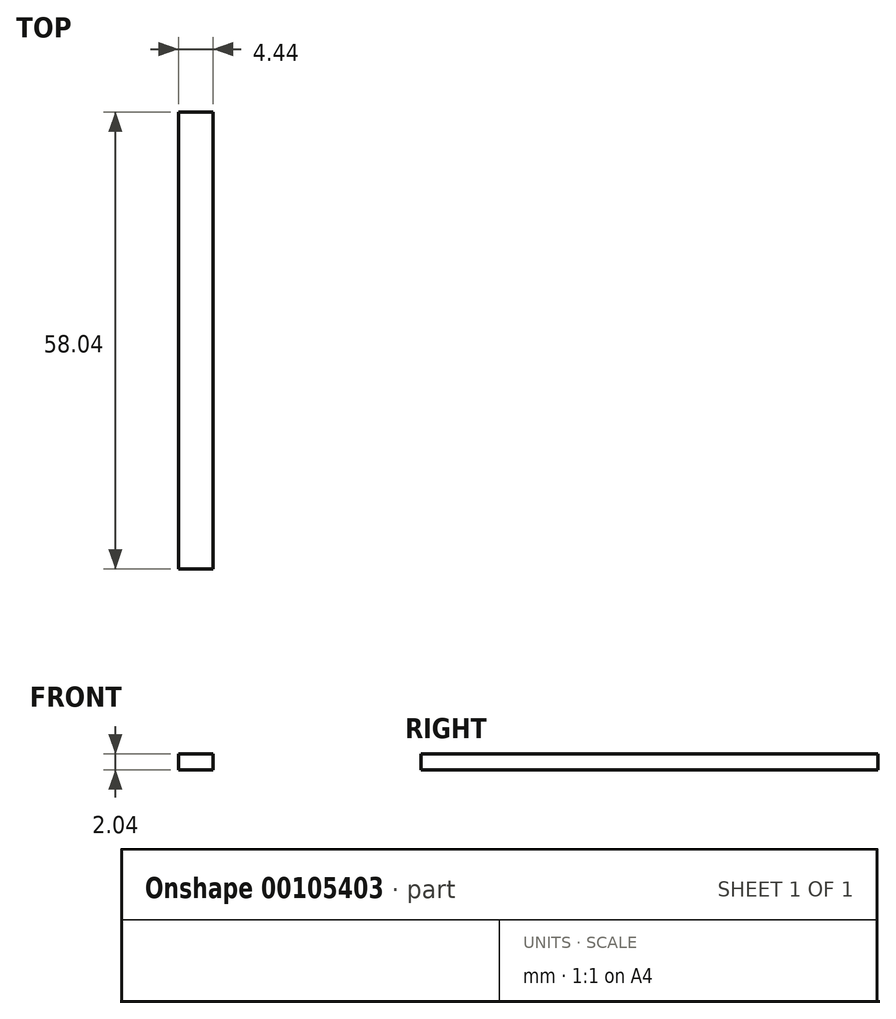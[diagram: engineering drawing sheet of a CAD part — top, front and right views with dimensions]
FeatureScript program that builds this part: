
annotation { "Feature Type Name" : "Feature", "Feature Type Description" : "" }
export const myFeature = defineFeature(function(context is Context, id is Id, definition is map)
    precondition{}
    {
        {
            var Q0;
            Q0=qCreatedBy(makeId("Front.planeOp"),FACE);
            var sketch = newSketch(context, id + "F0", { "sketchPlane" : qUnion([Q0])});
            skLineSegment(sketch, "E0.bottom", {"start": v(2.22, 1.02) * mm, "end": v(-2.22, 1.02) * mm});
            skLineSegment(sketch, "E0.top", {"start": v(2.22, -1.02) * mm, "end": v(-2.22, -1.02) * mm});
            skLineSegment(sketch, "E0.left", {"start": v(2.22, 1.02) * mm, "end": v(2.22, -1.02) * mm});
            skLineSegment(sketch, "E0.right", {"start": v(-2.22, 1.02) * mm, "end": v(-2.22, -1.02) * mm});
            skPoint(sketch, "E0.middle", {"position": v(0, 0) * mm});
            skSolve(sketch);
        }
        {
            var Q0;
            Q0=makeQuery(id+"F0.imprint","IMPRINT",FACE,{"disambiguationData":[TD([[makeQuery(id+"F0.imprint","IMPRINT",EDGE,{"derivedFrom":sQuery(id+"F0.wireOp",EDGE,"E0.bottom")}),1.0]])]});
            extrude(context, id + "F1", {"entities" : qUnion([Q0]), "depth" : 58.04 * mm});
        }
    });
